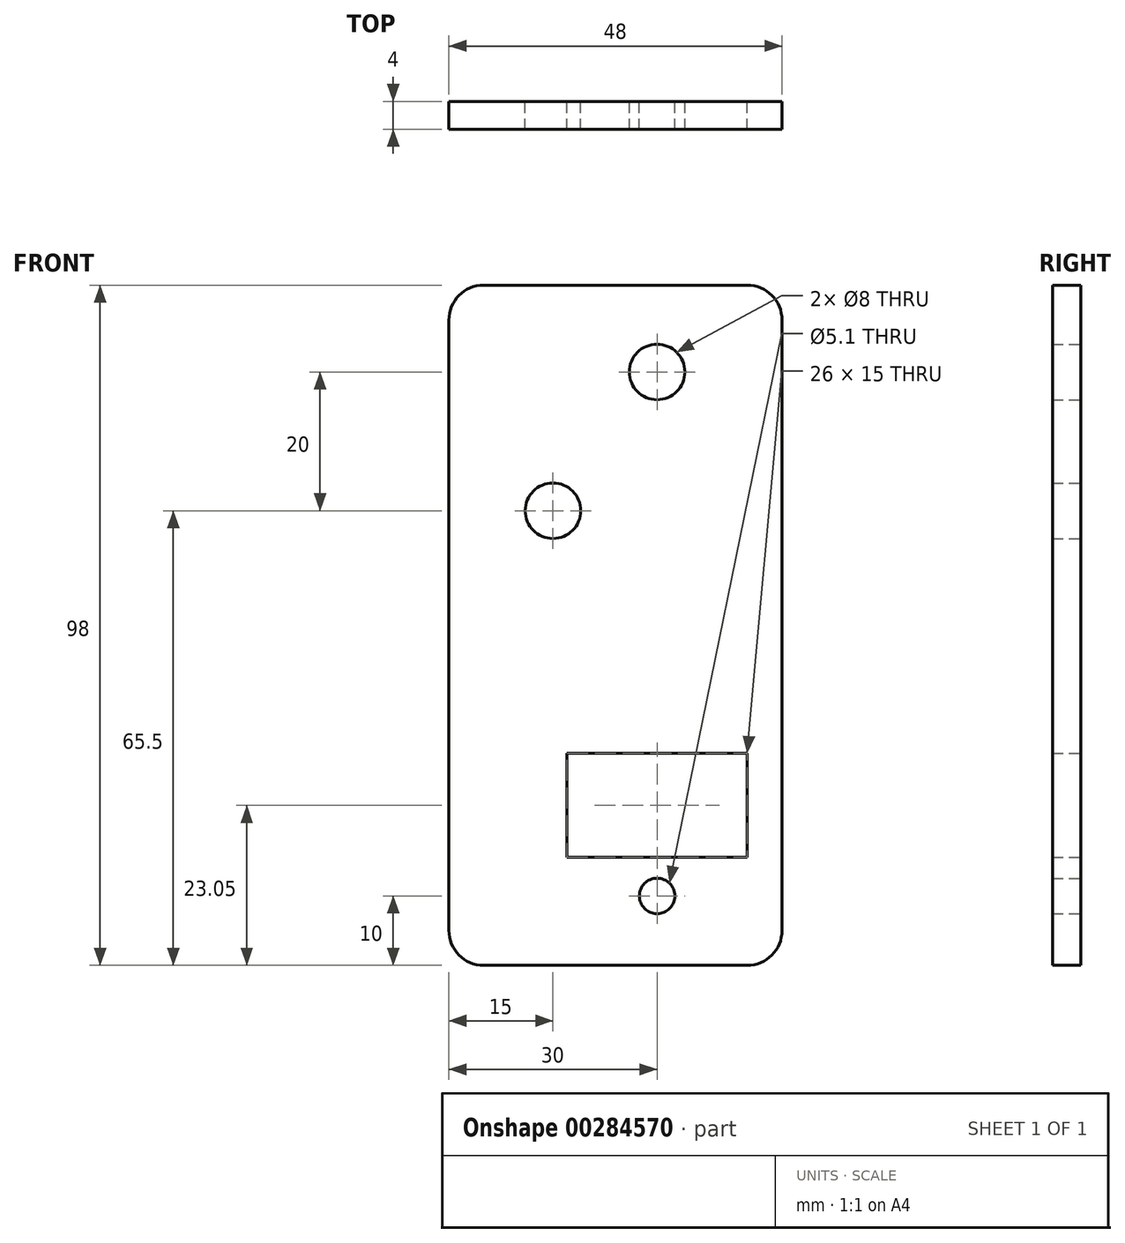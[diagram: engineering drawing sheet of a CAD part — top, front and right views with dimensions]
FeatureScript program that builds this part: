
annotation { "Feature Type Name" : "Feature", "Feature Type Description" : "" }
export const myFeature = defineFeature(function(context is Context, id is Id, definition is map)
    precondition{}
    {
        {
            var Q0;
            Q0=qCreatedBy(makeId("Front.planeOp"),FACE);
            var sketch = newSketch(context, id + "F0", { "sketchPlane" : qUnion([Q0])});
            skLineSegment(sketch, "E0", {"start": v(-17.5, 5) * mm, "end": v(-17.5, 93) * mm});
            skLineSegment(sketch, "E1", {"start": v(-12.5, 98) * mm, "end": v(25.5, 98) * mm});
            skLineSegment(sketch, "E2", {"start": v(30.5, 93) * mm, "end": v(30.5, 5) * mm});
            skLineSegment(sketch, "E3", {"start": v(25.5, 0) * mm, "end": v(-12.5, 0) * mm});
            skPoint(sketch, "E4", {"position": v(12.5, 10) * mm});
            skPoint(sketch, "E5", {"position": v(12.5, 85.5) * mm});
            skPoint(sketch, "E6", {"position": v(-2.5, 65.5) * mm});
            skPoint(sketch, "E7.visualSharp", {"position": v(-17.5, 98) * mm});
            skArc(sketch, "E7.filletArc", {"start": v(-12.5, 98) * mm, "mid": v(-16.04, 96.54) * mm, "end": v(-17.5, 93) * mm});
            skPoint(sketch, "E8.visualSharp", {"position": v(30.5, 98) * mm});
            skArc(sketch, "E8.filletArc", {"start": v(30.5, 93) * mm, "mid": v(29.04, 96.54) * mm, "end": v(25.5, 98) * mm});
            skPoint(sketch, "E9.visualSharp", {"position": v(0, 0) * mm});
            skPoint(sketch, "E10.visualSharp", {"position": v(30.5, 0) * mm});
            skArc(sketch, "E10.filletArc", {"start": v(25.5, 0) * mm, "mid": v(29.04, 1.46) * mm, "end": v(30.5, 5) * mm});
            skCircle(sketch, "E11", {"center": v(12.5, 10) * mm, "radius": 12.5 * mm, "construction": true});
            skLineSegment(sketch, "E12.bottom", {"start": v(-0.5, 30.55) * mm, "end": v(25.5, 30.55) * mm});
            skLineSegment(sketch, "E12.top", {"start": v(-0.5, 15.55) * mm, "end": v(25.5, 15.55) * mm});
            skLineSegment(sketch, "E12.left", {"start": v(-0.5, 30.55) * mm, "end": v(-0.5, 15.55) * mm});
            skLineSegment(sketch, "E12.right", {"start": v(25.5, 30.55) * mm, "end": v(25.5, 15.55) * mm});
            skCircle(sketch, "E13", {"center": v(12.5, 10) * mm, "radius": 2.55 * mm});
            skLineSegment(sketch, "E14", {"start": v(12.5, 2.98) * mm, "end": v(12.5, 22.5) * mm, "construction": true});
            skLineSegment(sketch, "E15", {"start": v(7.5, 21.46) * mm, "end": v(7.5, 4.2) * mm, "construction": true});
            skLineSegment(sketch, "E16", {"start": v(17.5, 21.46) * mm, "end": v(17.5, 2.98) * mm, "construction": true});
            skPoint(sketch, "E17.orphan", {"position": v(12.5, 25.52) * mm});
            skPoint(sketch, "E18.orphan", {"position": v(17.5, 25.52) * mm});
            skCircle(sketch, "E19", {"center": v(7.5, 21.46) * mm, "radius": 3.75 * mm, "construction": true});
            skCircle(sketch, "E20", {"center": v(17.5, 21.46) * mm, "radius": 3.75 * mm, "construction": true});
            skPoint(sketch, "E21.visualSharp", {"position": v(-17.5, 0) * mm});
            skArc(sketch, "E21.filletArc", {"start": v(-17.5, 5) * mm, "mid": v(-16.04, 1.46) * mm, "end": v(-12.5, 0) * mm});
            skCircle(sketch, "E22", {"center": v(-2.5, 65.5) * mm, "radius": 4 * mm});
            skCircle(sketch, "E23", {"center": v(12.5, 85.5) * mm, "radius": 4 * mm});
            skSolve(sketch);
        }
        {
            var Q0;
            Q0=qSketchRegion(id+"F0",true);
            extrude(context, id + "F1", {"entities" : qUnion([Q0]), "depth" : 4 * mm});
        }
    });
